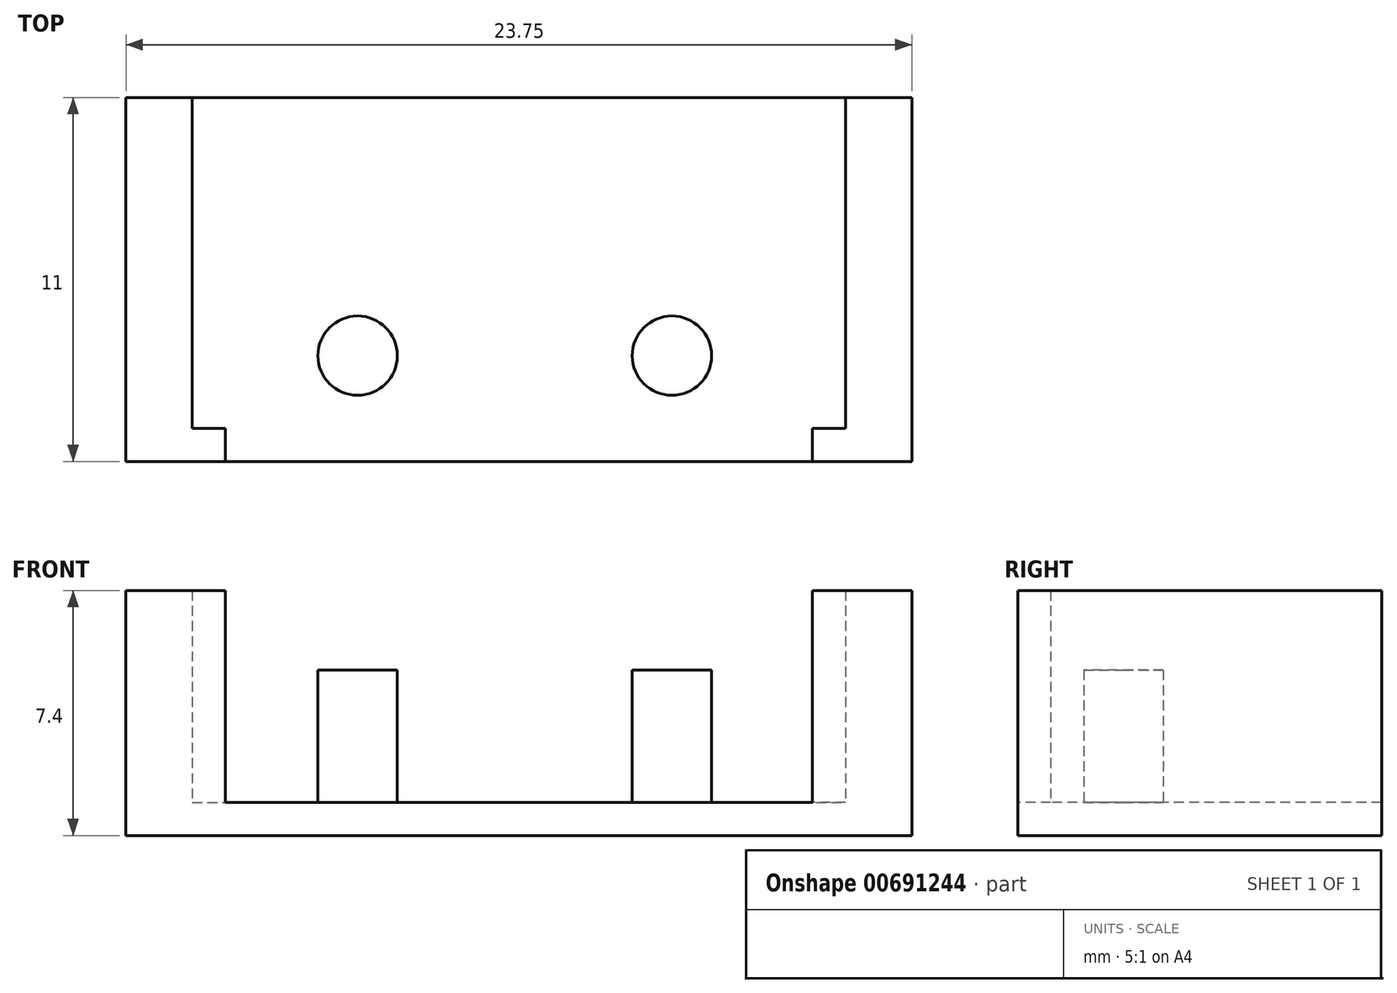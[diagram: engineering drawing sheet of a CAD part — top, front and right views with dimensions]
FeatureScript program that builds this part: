
annotation { "Feature Type Name" : "Feature", "Feature Type Description" : "" }
export const myFeature = defineFeature(function(context is Context, id is Id, definition is map)
    precondition{}
    {
        {
            var Q0;
            Q0=qCreatedBy(makeId("Top.planeOp"),FACE);
            var sketch = newSketch(context, id + "F0", { "sketchPlane" : qUnion([Q0])});
            skLineSegment(sketch, "E0.bottom", {"start": v(13.06, -8.22) * mm, "end": v(36.8, -8.22) * mm});
            skLineSegment(sketch, "E0.top", {"start": v(12.8, -19.22) * mm, "end": v(36.8, -19.22) * mm});
            skLineSegment(sketch, "E0.right", {"start": v(36.8, -8.22) * mm, "end": v(36.8, -19.22) * mm});
            skLineSegment(sketch, "E1", {"start": v(15.06, -8.22) * mm, "end": v(15.06, -18.22) * mm});
            skLineSegment(sketch, "E2", {"start": v(15.06, -18.22) * mm, "end": v(16.06, -18.22) * mm});
            skLineSegment(sketch, "E3", {"start": v(16.06, -18.22) * mm, "end": v(16.06, -19.22) * mm});
            skLineSegment(sketch, "E4", {"start": v(34.8, -8.22) * mm, "end": v(34.8, -18.22) * mm});
            skLineSegment(sketch, "E5", {"start": v(34.8, -18.22) * mm, "end": v(33.8, -18.22) * mm});
            skLineSegment(sketch, "E6", {"start": v(33.8, -18.22) * mm, "end": v(33.8, -19.22) * mm});
            skLineSegment(sketch, "E7", {"start": v(12.22, -19.22) * mm, "end": v(12.22, -16.02) * mm});
            skLineSegment(sketch, "E8", {"start": v(38.86, -19.22) * mm, "end": v(38.86, -16.02) * mm});
            skLineSegment(sketch, "E9", {"start": v(12.22, -16.02) * mm, "end": v(38.86, -16.02) * mm, "construction": true});
            skLineSegment(sketch, "E10", {"start": v(34.8, -14.47) * mm, "end": v(29.56, -14.47) * mm, "construction": true});
            skCircle(sketch, "E11", {"center": v(20.06, -16.02) * mm, "radius": 1.2 * mm});
            skCircle(sketch, "E12", {"center": v(29.56, -16.02) * mm, "radius": 1.2 * mm});
            skLineSegment(sketch, "E13", {"start": v(13.06, -8.22) * mm, "end": v(13.06, -19.22) * mm});
            skLineSegment(sketch, "E14", {"start": v(15.06, -14.52) * mm, "end": v(20.06, -14.52) * mm, "construction": true});
            skSolve(sketch);
        }
        {
            var Q0;
            {var subQ0=sQuery(id+"F0.wireOp",EDGE,"E1");Q0=makeQuery(id+"F0.imprint","IMPRINT",FACE,{"disambiguationData":[TD([[makeQuery(id+"F0.imprint","IMPRINT",EDGE,{"derivedFrom":subQ0}),1.0]])]});}
            extrude(context, id + "F1", {"entities" : qUnion([Q0]), "depth" : 1 * mm, "offsetDistance" : 25 * mm});
        }
        {
            var Q0;
            {var subQ0=sQuery(id+"F0.wireOp",EDGE,"E1");Q0=makeQuery(id+"F0.imprint","IMPRINT",FACE,{"disambiguationData":[TD([[makeQuery(id+"F0.imprint","IMPRINT",EDGE,{"derivedFrom":subQ0}),-1.0]])]});}
            var Q1;
            {var subQ0=sQuery(id+"F0.wireOp",EDGE,"E0.right");Q1=makeQuery(id+"F0.imprint","IMPRINT",FACE,{"disambiguationData":[TD([[makeQuery(id+"F0.imprint","IMPRINT",EDGE,{"derivedFrom":subQ0}),-1.0]])]});}
            extrude(context, id + "F2", {"entities" : qUnion([Q0, Q1]), "operationType" : NewBodyOperationType.ADD, "depth" : 7.4 * mm, "offsetDistance" : 25 * mm});
        }
        {
            var Q0;
            Q0=makeQuery(id+"F0.imprint","IMPRINT",FACE,{"disambiguationData":[TD([[makeQuery(id+"F0.imprint","IMPRINT",EDGE,{"derivedFrom":sQuery(id+"F0.wireOp",EDGE,"E11")}),1.0]])]});
            var Q1;
            Q1=makeQuery(id+"F0.imprint","IMPRINT",FACE,{"disambiguationData":[TD([[makeQuery(id+"F0.imprint","IMPRINT",EDGE,{"derivedFrom":sQuery(id+"F0.wireOp",EDGE,"E12")}),1.0]])]});
            extrude(context, id + "F3", {"entities" : qUnion([Q0, Q1]), "operationType" : NewBodyOperationType.ADD, "depth" : 5 * mm, "offsetDistance" : 25 * mm});
        }
    });
